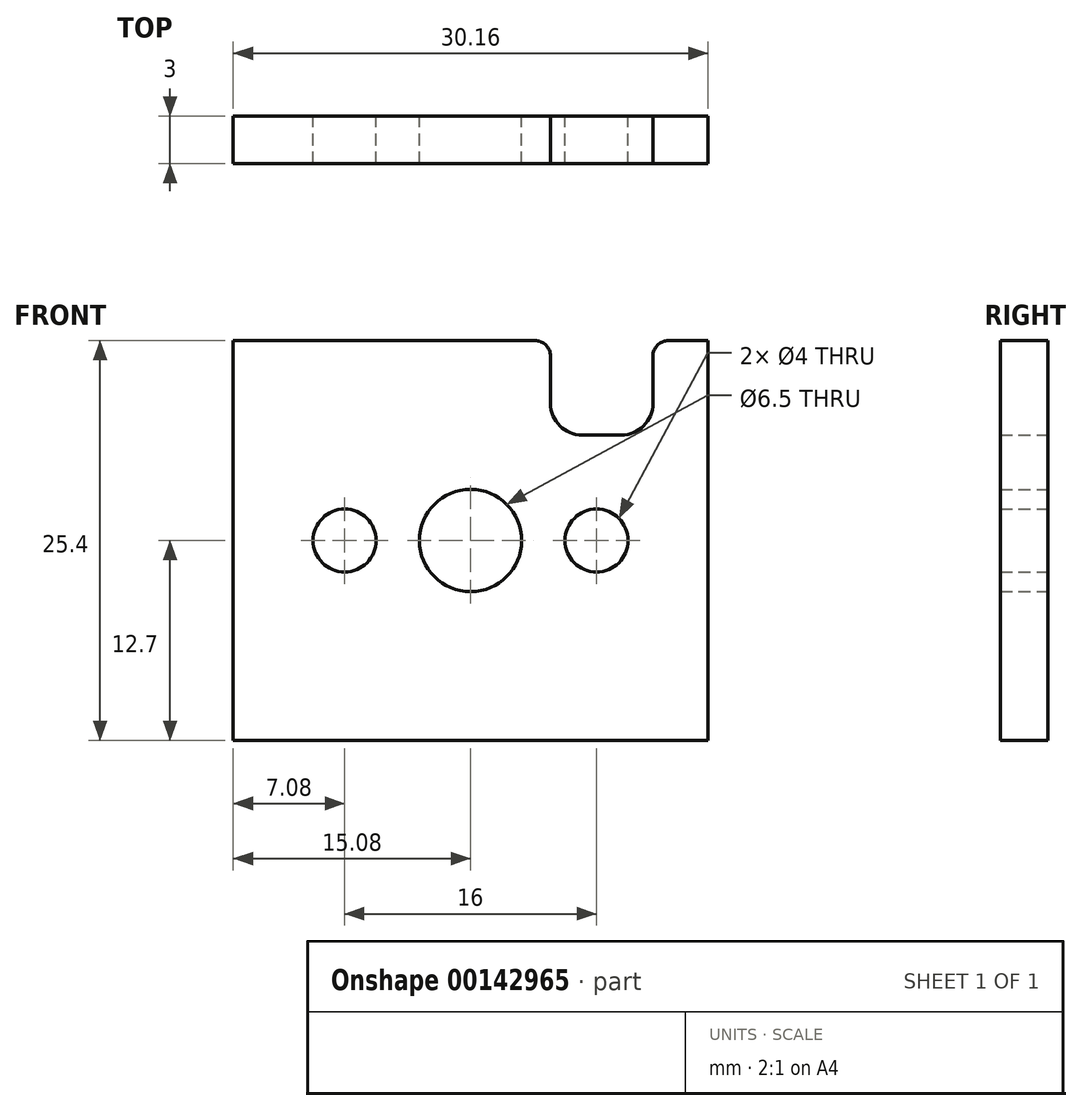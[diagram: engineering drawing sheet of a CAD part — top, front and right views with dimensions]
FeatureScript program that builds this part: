
annotation { "Feature Type Name" : "Feature", "Feature Type Description" : "" }
export const myFeature = defineFeature(function(context is Context, id is Id, definition is map)
    precondition{}
    {
        {
            var Q0;
            Q0=qCreatedBy(makeId("Front.planeOp"),FACE);
            var sketch = newSketch(context, id + "F0", { "sketchPlane" : qUnion([Q0])});
            skLineSegment(sketch, "E0.bottom", {"start": v(15.08, -12.7) * mm, "end": v(-15.08, -12.7) * mm});
            skLineSegment(sketch, "E0.top", {"start": v(15.08, 12.7) * mm, "end": v(12.58, 12.7) * mm});
            skLineSegment(sketch, "E0.left", {"start": v(15.08, -12.7) * mm, "end": v(15.08, 12.7) * mm});
            skLineSegment(sketch, "E0.right", {"start": v(-15.08, -12.7) * mm, "end": v(-15.08, 12.7) * mm});
            skPoint(sketch, "E0.middle", {"position": v(0, 0) * mm});
            skCircle(sketch, "E1", {"center": v(0, 0) * mm, "radius": 3.25 * mm});
            skLineSegment(sketch, "E2.0", {"start": v(11.58, 8.7) * mm, "end": v(11.58, 11.7) * mm});
            skLineSegment(sketch, "E3.0", {"start": v(5.08, 8.7) * mm, "end": v(5.08, 11.7) * mm});
            skLineSegment(sketch, "E4.0", {"start": v(9.58, 6.7) * mm, "end": v(7.08, 6.7) * mm});
            skLineSegment(sketch, "E5.trimOffspring", {"start": v(4.08, 12.7) * mm, "end": v(-15.08, 12.7) * mm});
            skPoint(sketch, "E6.visualSharp", {"position": v(5.08, 6.7) * mm});
            skArc(sketch, "E6.filletArc", {"start": v(5.08, 8.7) * mm, "mid": v(5.67, 7.29) * mm, "end": v(7.08, 6.7) * mm});
            skPoint(sketch, "E7.visualSharp", {"position": v(11.58, 6.7) * mm});
            skArc(sketch, "E7.filletArc", {"start": v(9.58, 6.7) * mm, "mid": v(11, 7.29) * mm, "end": v(11.58, 8.7) * mm});
            skPoint(sketch, "E8.visualSharp", {"position": v(5.08, 12.7) * mm});
            skArc(sketch, "E8.filletArc", {"start": v(5.08, 11.7) * mm, "mid": v(4.79, 12.4) * mm, "end": v(4.08, 12.7) * mm});
            skPoint(sketch, "E9.visualSharp", {"position": v(11.58, 12.7) * mm});
            skArc(sketch, "E9.filletArc", {"start": v(12.58, 12.7) * mm, "mid": v(11.87, 12.4) * mm, "end": v(11.58, 11.7) * mm});
            skLineSegment(sketch, "E10", {"start": v(0, 0) * mm, "end": v(-8, 0) * mm});
            skLineSegment(sketch, "E11", {"start": v(0, 0) * mm, "end": v(8, 0) * mm});
            skCircle(sketch, "E12", {"center": v(-8, 0) * mm, "radius": 2 * mm});
            skCircle(sketch, "E13", {"center": v(8, 0) * mm, "radius": 2 * mm});
            skSolve(sketch);
        }
        {
            var Q0;
            Q0 = qSketchRegion(id + "F0", true);
            extrude(context, id + "F1", {"entities" : qUnion([Q0]), "depth" : 3 * mm});
        }
    });
